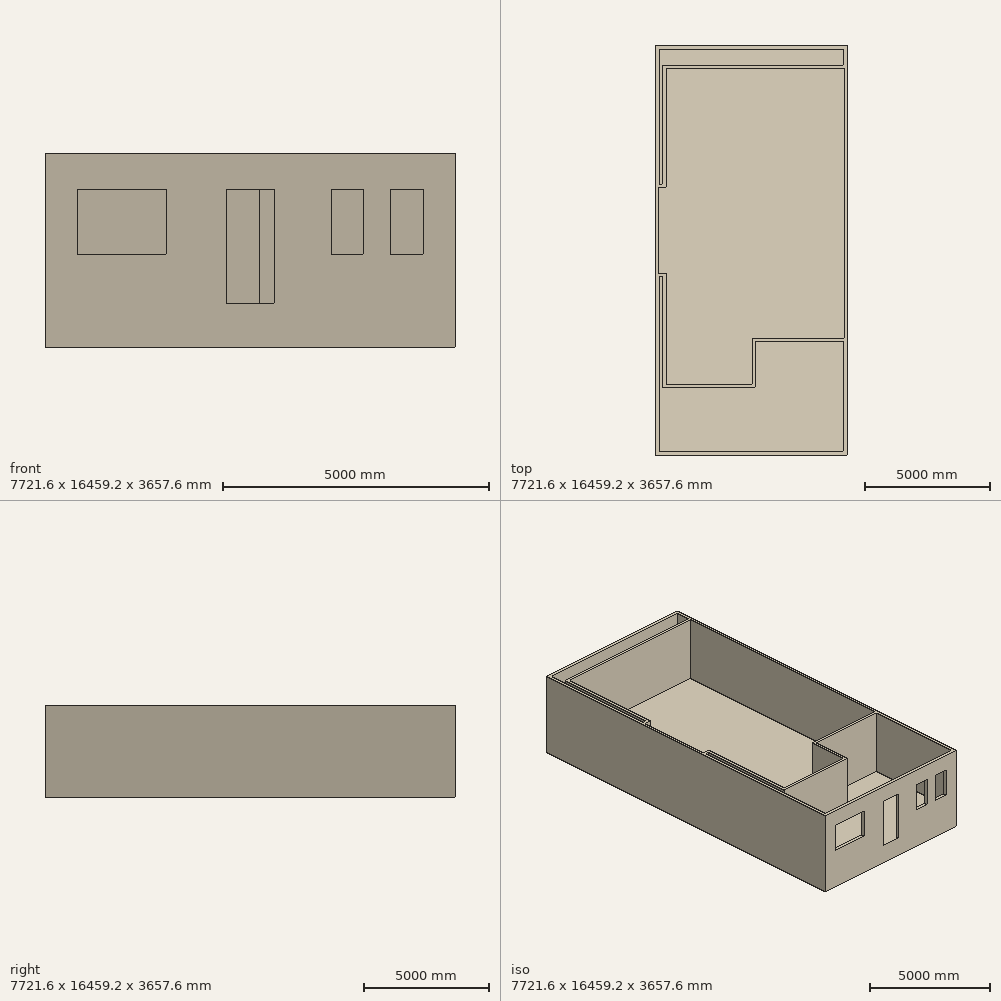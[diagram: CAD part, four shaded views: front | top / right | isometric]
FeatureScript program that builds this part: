
annotation { "Feature Type Name" : "Feature", "Feature Type Description" : "" }
export const myFeature = defineFeature(function(context is Context, id is Id, definition is map)
    precondition{}
    {
        {
            var Q0;
            Q0=qCreatedBy(makeId("Top.planeOp"),FACE);
            var sketch = newSketch(context, id + "F0", { "sketchPlane" : qUnion([Q0])});
            skLineSegment(sketch, "E0", {"start": v(3683, 0) * mm, "end": v(3683, 11099.8) * mm});
            skLineSegment(sketch, "E1", {"start": v(3683, 11099.8) * mm, "end": v(-3733.8, 11099.8) * mm});
            skLineSegment(sketch, "E2", {"start": v(-3733.8, 11099.8) * mm, "end": v(-3733.8, 6324.6) * mm});
            skLineSegment(sketch, "E3", {"start": v(-3733.8, 6324.6) * mm, "end": v(-4038.6, 6324.6) * mm});
            skLineSegment(sketch, "E4", {"start": v(-4038.6, 6324.6) * mm, "end": v(-4038.6, 2616.2) * mm});
            skLineSegment(sketch, "E5", {"start": v(-4038.6, 2616.2) * mm, "end": v(-3733.8, 2616.2) * mm});
            skLineSegment(sketch, "E6", {"start": v(-3733.8, 2616.2) * mm, "end": v(-3733.8, -1828.8) * mm});
            skLineSegment(sketch, "E7", {"start": v(0, -1828.8) * mm, "end": v(0, 0) * mm});
            skLineSegment(sketch, "E8", {"start": v(0, 0) * mm, "end": v(3683, 0) * mm});
            skPoint(sketch, "E9.orphan", {"position": v(3683, 0) * mm});
            skLineSegment(sketch, "E10", {"start": v(-3733.8, -1828.8) * mm, "end": v(0, -1828.8) * mm});
            skLineSegment(sketch, "E11.0", {"start": v(-127, -1701.8) * mm, "end": v(-127, 127) * mm});
            skLineSegment(sketch, "E11.1", {"start": v(-3606.8, -1701.8) * mm, "end": v(-127, -1701.8) * mm});
            skLineSegment(sketch, "E11.2", {"start": v(-3606.8, 2743.2) * mm, "end": v(-3606.8, -1701.8) * mm});
            skLineSegment(sketch, "E11.3", {"start": v(-3911.6, 2743.2) * mm, "end": v(-3606.8, 2743.2) * mm});
            skLineSegment(sketch, "E11.4", {"start": v(-3911.6, 6197.6) * mm, "end": v(-3911.6, 2743.2) * mm});
            skLineSegment(sketch, "E11.5", {"start": v(-127, 127) * mm, "end": v(3556, 127) * mm});
            skLineSegment(sketch, "E11.6", {"start": v(-3606.8, 6197.6) * mm, "end": v(-3911.6, 6197.6) * mm});
            skLineSegment(sketch, "E11.7", {"start": v(-3606.8, 10972.8) * mm, "end": v(-3606.8, 6197.6) * mm});
            skLineSegment(sketch, "E11.8", {"start": v(3556, 10972.8) * mm, "end": v(-3606.8, 10972.8) * mm});
            skLineSegment(sketch, "E11.9", {"start": v(3556, 127) * mm, "end": v(3556, 10972.8) * mm});
            skLineSegment(sketch, "E12.bottom", {"start": v(-3746.5, 438.15) * mm, "end": v(-3594.1, 438.15) * mm, "construction": true});
            skLineSegment(sketch, "E12.top", {"start": v(-3746.5, 1352.55) * mm, "end": v(-3594.1, 1352.55) * mm, "construction": true});
            skLineSegment(sketch, "E12.left", {"start": v(-3746.5, 438.15) * mm, "end": v(-3746.5, 1352.55) * mm, "construction": true});
            skLineSegment(sketch, "E12.right", {"start": v(-3594.1, 438.15) * mm, "end": v(-3594.1, 1352.55) * mm, "construction": true});
            skLineSegment(sketch, "E13", {"start": v(-3606.8, 2609.85) * mm, "end": v(-2933.7, 2609.85) * mm, "construction": true});
            skLineSegment(sketch, "E14", {"start": v(-2933.7, 2609.85) * mm, "end": v(-2933.7, 2743.2) * mm, "construction": true});
            skLineSegment(sketch, "E15", {"start": v(-2933.7, 2743.2) * mm, "end": v(-3606.8, 2743.2) * mm, "construction": true});
            skLineSegment(sketch, "E16.bottom", {"start": v(-2705.1, -1689.1) * mm, "end": v(-1054.1, -1689.1) * mm, "construction": true});
            skLineSegment(sketch, "E16.top", {"start": v(-2705.1, -1841.5) * mm, "end": v(-1054.1, -1841.5) * mm, "construction": true});
            skLineSegment(sketch, "E16.left", {"start": v(-2705.1, -1689.1) * mm, "end": v(-2705.1, -1841.5) * mm, "construction": true});
            skLineSegment(sketch, "E16.right", {"start": v(-1054.1, -1689.1) * mm, "end": v(-1054.1, -1841.5) * mm, "construction": true});
            skLineSegment(sketch, "E17", {"start": v(-127, 127) * mm, "end": v(-127, 2609.85) * mm, "construction": true});
            skLineSegment(sketch, "E18", {"start": v(-127, 2609.85) * mm, "end": v(-800.1, 2609.85) * mm, "construction": true});
            skLineSegment(sketch, "E19", {"start": v(-800.1, 2743.2) * mm, "end": v(-88.9, 2743.2) * mm, "construction": true});
            skLineSegment(sketch, "E20", {"start": v(-88.9, 2743.2) * mm, "end": v(660.4, 3359.05) * mm, "construction": true});
            skLineSegment(sketch, "E21", {"start": v(660.4, 3359.05) * mm, "end": v(660.4, 5268.85) * mm, "construction": true});
            skLineSegment(sketch, "E22", {"start": v(0, 127) * mm, "end": v(0, 2680.36) * mm, "construction": true});
            skLineSegment(sketch, "E23", {"start": v(76.33, 2747.5) * mm, "end": v(800.1, 1866.9) * mm, "construction": true});
            skLineSegment(sketch, "E24", {"start": v(800.1, 1866.9) * mm, "end": v(800.1, 127) * mm, "construction": true});
            skLineSegment(sketch, "E25", {"start": v(-800.1, 2743.2) * mm, "end": v(-800.1, 2609.85) * mm});
            skLineSegment(sketch, "E26", {"start": v(76.33, 2747.5) * mm, "end": v(812.8, 3352.8) * mm, "construction": true});
            skLineSegment(sketch, "E27", {"start": v(812.8, 3352.8) * mm, "end": v(3556, 3352.8) * mm, "construction": true});
            skLineSegment(sketch, "E28", {"start": v(3556, 3479.8) * mm, "end": v(787.4, 3479.8) * mm, "construction": true});
            skLineSegment(sketch, "E29", {"start": v(787.4, 3479.8) * mm, "end": v(787.4, 5181.6) * mm, "construction": true});
            skLineSegment(sketch, "E30", {"start": v(787.4, 5181.6) * mm, "end": v(3556, 5181.6) * mm, "construction": true});
            skLineSegment(sketch, "E31", {"start": v(3541.89, 5308.6) * mm, "end": v(781.97, 5308.6) * mm, "construction": true});
            skLineSegment(sketch, "E32", {"start": v(781.97, 5308.6) * mm, "end": v(0, 5845.85) * mm, "construction": true});
            skLineSegment(sketch, "E33", {"start": v(0, 8534.4) * mm, "end": v(698.5, 8534.4) * mm, "construction": true});
            skLineSegment(sketch, "E34", {"start": v(660.4, 5268.85) * mm, "end": v(-293.97, 5924.55) * mm, "construction": true});
            skLineSegment(sketch, "E35", {"start": v(-293.97, 5924.55) * mm, "end": v(-293.97, 6197.6) * mm, "construction": true});
            skLineSegment(sketch, "E36", {"start": v(-293.97, 6197.6) * mm, "end": v(-3606.8, 6197.6) * mm, "construction": true});
            skLineSegment(sketch, "E37.bottom", {"start": v(1346.2, 139.7) * mm, "end": v(2070.1, 139.7) * mm, "construction": true});
            skLineSegment(sketch, "E37.top", {"start": v(1346.2, -12.7) * mm, "end": v(2070.1, -12.7) * mm, "construction": true});
            skLineSegment(sketch, "E37.left", {"start": v(1346.2, 139.7) * mm, "end": v(1346.2, -12.7) * mm, "construction": true});
            skLineSegment(sketch, "E37.right", {"start": v(2070.1, 139.7) * mm, "end": v(2070.1, -12.7) * mm, "construction": true});
            skLineSegment(sketch, "E38.bottom", {"start": v(3543.3, 2781.3) * mm, "end": v(3695.7, 2781.3) * mm, "construction": true});
            skLineSegment(sketch, "E38.top", {"start": v(3543.3, 2051.05) * mm, "end": v(3695.7, 2051.05) * mm, "construction": true});
            skLineSegment(sketch, "E38.left", {"start": v(3543.3, 2781.3) * mm, "end": v(3543.3, 2051.05) * mm, "construction": true});
            skLineSegment(sketch, "E38.right", {"start": v(3695.7, 2781.3) * mm, "end": v(3695.7, 2051.05) * mm, "construction": true});
            skLineSegment(sketch, "E39", {"start": v(0, 2680.36) * mm, "end": v(698.5, 1830.5) * mm, "construction": true});
            skLineSegment(sketch, "E40", {"start": v(698.5, 1830.5) * mm, "end": v(698.5, 127) * mm, "construction": true});
            skLineSegment(sketch, "E41.bottom", {"start": v(3543.3, 4610.1) * mm, "end": v(3695.7, 4610.1) * mm, "construction": true});
            skLineSegment(sketch, "E41.top", {"start": v(3543.3, 4038.6) * mm, "end": v(3695.7, 4038.6) * mm, "construction": true});
            skLineSegment(sketch, "E41.left", {"start": v(3543.3, 4610.1) * mm, "end": v(3543.3, 4038.6) * mm, "construction": true});
            skLineSegment(sketch, "E41.right", {"start": v(3695.7, 4610.1) * mm, "end": v(3695.7, 4038.6) * mm, "construction": true});
            skLineSegment(sketch, "E42.bottom", {"start": v(635, 4394.2) * mm, "end": v(787.4, 4394.2) * mm, "construction": true});
            skLineSegment(sketch, "E42.top", {"start": v(635, 3632.2) * mm, "end": v(787.4, 3632.2) * mm, "construction": true});
            skLineSegment(sketch, "E42.left", {"start": v(635, 4394.2) * mm, "end": v(635, 3632.2) * mm, "construction": true});
            skLineSegment(sketch, "E42.right", {"start": v(787.4, 4394.2) * mm, "end": v(787.4, 3632.2) * mm, "construction": true});
            skLineSegment(sketch, "E43.bottom", {"start": v(-427.32, 6172.2) * mm, "end": v(-1189.32, 6172.2) * mm, "construction": true});
            skLineSegment(sketch, "E43.top", {"start": v(-427.32, 6324.6) * mm, "end": v(-1189.32, 6324.6) * mm, "construction": true});
            skLineSegment(sketch, "E43.left", {"start": v(-427.32, 6172.2) * mm, "end": v(-427.32, 6324.6) * mm, "construction": true});
            skLineSegment(sketch, "E43.right", {"start": v(-1189.32, 6172.2) * mm, "end": v(-1189.32, 6324.6) * mm, "construction": true});
            skLineSegment(sketch, "E44.bottom", {"start": v(-4064, 3619.5) * mm, "end": v(-3911.6, 3619.5) * mm, "construction": true});
            skLineSegment(sketch, "E44.top", {"start": v(-4064, 4349.75) * mm, "end": v(-3911.6, 4349.75) * mm, "construction": true});
            skLineSegment(sketch, "E44.left", {"start": v(-4064, 3619.5) * mm, "end": v(-4064, 4349.75) * mm, "construction": true});
            skLineSegment(sketch, "E44.right", {"start": v(-3911.6, 3619.5) * mm, "end": v(-3911.6, 4349.75) * mm, "construction": true});
            skLineSegment(sketch, "E45.bottom", {"start": v(3543.3, 5867.4) * mm, "end": v(3695.7, 5867.4) * mm, "construction": true});
            skLineSegment(sketch, "E45.top", {"start": v(3543.3, 7061.2) * mm, "end": v(3695.7, 7061.2) * mm, "construction": true});
            skLineSegment(sketch, "E45.left", {"start": v(3543.3, 5867.4) * mm, "end": v(3543.3, 7061.2) * mm, "construction": true});
            skLineSegment(sketch, "E45.right", {"start": v(3695.7, 5867.4) * mm, "end": v(3695.7, 7061.2) * mm, "construction": true});
            skLineSegment(sketch, "E46.bottom", {"start": v(3543.3, 9438.28) * mm, "end": v(3695.7, 9438.28) * mm, "construction": true});
            skLineSegment(sketch, "E46.top", {"start": v(3543.3, 10256.66) * mm, "end": v(3695.7, 10256.66) * mm, "construction": true});
            skLineSegment(sketch, "E46.left", {"start": v(3543.3, 9438.28) * mm, "end": v(3543.3, 10256.66) * mm, "construction": true});
            skLineSegment(sketch, "E46.right", {"start": v(3695.7, 9438.28) * mm, "end": v(3695.7, 10256.66) * mm, "construction": true});
            skLineSegment(sketch, "E47.bottom", {"start": v(2881.46, 10778.72) * mm, "end": v(1984.95, 10778.72) * mm, "construction": true});
            skLineSegment(sketch, "E47.top", {"start": v(2881.46, 10931.12) * mm, "end": v(1984.95, 10931.12) * mm, "construction": true});
            skLineSegment(sketch, "E47.left", {"start": v(2881.46, 10778.72) * mm, "end": v(2881.46, 10931.12) * mm, "construction": true});
            skLineSegment(sketch, "E47.right", {"start": v(1984.95, 10778.72) * mm, "end": v(1984.95, 10931.12) * mm, "construction": true});
            skLineSegment(sketch, "E48.bottom", {"start": v(1766.71, 10778.72) * mm, "end": v(966.52, 10778.72) * mm, "construction": true});
            skLineSegment(sketch, "E48.top", {"start": v(1766.71, 10931.12) * mm, "end": v(966.52, 10931.12) * mm, "construction": true});
            skLineSegment(sketch, "E48.left", {"start": v(1766.71, 10778.72) * mm, "end": v(1766.71, 10931.12) * mm, "construction": true});
            skLineSegment(sketch, "E48.right", {"start": v(966.52, 10778.72) * mm, "end": v(966.52, 10931.12) * mm, "construction": true});
            skLineSegment(sketch, "E49.bottom", {"start": v(-1415.88, 10778.72) * mm, "end": v(-2525.25, 10778.72) * mm, "construction": true});
            skLineSegment(sketch, "E49.top", {"start": v(-1415.88, 10931.12) * mm, "end": v(-2525.25, 10931.12) * mm, "construction": true});
            skLineSegment(sketch, "E49.left", {"start": v(-1415.88, 10778.72) * mm, "end": v(-1415.88, 10931.12) * mm, "construction": true});
            skLineSegment(sketch, "E49.right", {"start": v(-2525.25, 10778.72) * mm, "end": v(-2525.25, 10931.12) * mm, "construction": true});
            skPoint(sketch, "E50.oppositeSnap0", {"position": v(-3606.8, 8585.2) * mm});
            skLineSegment(sketch, "E50.bottom", {"start": v(-3936.87, 7828.6) * mm, "end": v(-4089.27, 7828.6) * mm, "construction": true});
            skLineSegment(sketch, "E50.top", {"start": v(-3936.87, 8585.2) * mm, "end": v(-4089.27, 8585.2) * mm, "construction": true});
            skLineSegment(sketch, "E50.left", {"start": v(-3936.87, 7828.6) * mm, "end": v(-3936.87, 8585.2) * mm, "construction": true});
            skLineSegment(sketch, "E50.right", {"start": v(-4089.27, 7828.6) * mm, "end": v(-4089.27, 8585.2) * mm, "construction": true});
            skLineSegment(sketch, "E51", {"start": v(-3606.8, 6299.2) * mm, "end": v(-293.97, 6299.2) * mm, "construction": true});
            skLineSegment(sketch, "E52", {"start": v(-293.97, 6299.2) * mm, "end": v(-293.97, 9093.2) * mm, "construction": true});
            skLineSegment(sketch, "E53", {"start": v(-293.97, 9093.2) * mm, "end": v(-805.07, 9093.2) * mm, "construction": true});
            skLineSegment(sketch, "E54", {"start": v(-805.07, 9093.2) * mm, "end": v(-805.07, 9245.6) * mm, "construction": true});
            skLineSegment(sketch, "E55", {"start": v(-805.07, 9245.6) * mm, "end": v(-293.97, 9245.6) * mm, "construction": true});
            skLineSegment(sketch, "E56", {"start": v(-293.97, 9245.6) * mm, "end": v(-293.97, 10972.8) * mm, "construction": true});
            skLineSegment(sketch, "E57", {"start": v(-107.65, 5765.72) * mm, "end": v(520.4, 5334.22) * mm, "construction": true});
            skLineSegment(sketch, "E58", {"start": v(520.4, 5334.22) * mm, "end": v(606.7, 5459.83) * mm, "construction": true});
            skLineSegment(sketch, "E59", {"start": v(606.7, 5459.83) * mm, "end": v(-21.35, 5891.33) * mm, "construction": true});
            skLineSegment(sketch, "E60", {"start": v(-21.35, 5891.33) * mm, "end": v(-107.65, 5765.72) * mm, "construction": true});
            skLineSegment(sketch, "E61", {"start": v(50.34, 2893.8) * mm, "end": v(639.02, 3377.65) * mm, "construction": true});
            skLineSegment(sketch, "E62", {"start": v(639.02, 3377.65) * mm, "end": v(735.79, 3259.91) * mm, "construction": true});
            skLineSegment(sketch, "E63", {"start": v(735.79, 3259.91) * mm, "end": v(147.1, 2776.07) * mm, "construction": true});
            skLineSegment(sketch, "E64", {"start": v(147.1, 2776.07) * mm, "end": v(50.34, 2893.8) * mm, "construction": true});
            skLineSegment(sketch, "E65", {"start": v(800.1, 8534.4) * mm, "end": v(800.1, 7010.4) * mm, "construction": true});
            skLineSegment(sketch, "E66", {"start": v(800.1, 7010.4) * mm, "end": v(0, 5845.85) * mm, "construction": true});
            skLineSegment(sketch, "E67", {"start": v(0, 6025.27) * mm, "end": v(698.5, 7041.94) * mm, "construction": true});
            skLineSegment(sketch, "E68", {"start": v(698.5, 7041.94) * mm, "end": v(698.5, 8534.4) * mm, "construction": true});
            skLineSegment(sketch, "E69.bottom", {"start": v(-4064, 4527.55) * mm, "end": v(-3911.6, 4527.55) * mm, "construction": true});
            skLineSegment(sketch, "E69.top", {"start": v(-4064, 5257.8) * mm, "end": v(-3911.6, 5257.8) * mm, "construction": true});
            skLineSegment(sketch, "E69.left", {"start": v(-4064, 4527.55) * mm, "end": v(-4064, 5257.8) * mm, "construction": true});
            skLineSegment(sketch, "E69.right", {"start": v(-3911.6, 4527.55) * mm, "end": v(-3911.6, 5257.8) * mm, "construction": true});
            skLineSegment(sketch, "E70.trimOffspring", {"start": v(800.1, 8534.4) * mm, "end": v(3556, 8534.4) * mm, "construction": true});
            skLineSegment(sketch, "E71", {"start": v(0, 8686.8) * mm, "end": v(3556, 8686.8) * mm, "construction": true});
            skLineSegment(sketch, "E72.trimOffspring", {"start": v(0, 6025.27) * mm, "end": v(0, 8534.4) * mm, "construction": true});
            skLineSegment(sketch, "E73.trimOffspring", {"start": v(0, 8686.8) * mm, "end": v(0, 10972.8) * mm, "construction": true});
            skSolve(sketch);
        }
        {
            var Q0;
            Q0=qSketchRegion(id+"F0",true);
            extrude(context, id + "F1", {"entities" : qUnion([Q0]), "depth" : 3657.6 * mm});
        }
        {
            var Q0;
            Q0=qCreatedBy(makeId("Top.planeOp"),FACE);
            var sketch = newSketch(context, id + "F2", { "sketchPlane" : qUnion([Q0])});
            skLineSegment(sketch, "E74.bottom", {"start": v(3683, -4572) * mm, "end": v(-4038.6, -4572) * mm});
            skLineSegment(sketch, "E74.top", {"start": v(3683, 11887.2) * mm, "end": v(-4038.6, 11887.2) * mm});
            skLineSegment(sketch, "E74.left", {"start": v(3683, -4572) * mm, "end": v(3683, 0) * mm});
            skLineSegment(sketch, "E74.right", {"start": v(-4038.6, -4572) * mm, "end": v(-4038.6, 2616.2) * mm});
            skLineSegment(sketch, "E75.0", {"start": v(3530.6, 11734.8) * mm, "end": v(-3886.2, 11734.8) * mm});
            skLineSegment(sketch, "E75.1", {"start": v(-3886.2, -4419.6) * mm, "end": v(-3886.2, 2616.2) * mm});
            skLineSegment(sketch, "E75.2", {"start": v(3530.6, -4419.6) * mm, "end": v(-3886.2, -4419.6) * mm});
            skLineSegment(sketch, "E75.3", {"start": v(3530.6, -4419.6) * mm, "end": v(3530.6, 0) * mm});
            skLineSegment(sketch, "E76", {"start": v(3530.6, 0) * mm, "end": v(3683, 0) * mm});
            skLineSegment(sketch, "E77", {"start": v(-4038.6, 2616.2) * mm, "end": v(-3886.2, 2616.2) * mm});
            skLineSegment(sketch, "E78", {"start": v(-4038.6, 6324.6) * mm, "end": v(-3886.2, 6324.6) * mm});
            skLineSegment(sketch, "E79.trimOffspring", {"start": v(-3886.2, 6324.6) * mm, "end": v(-3886.2, 11734.8) * mm});
            skLineSegment(sketch, "E80.trimOffspring", {"start": v(-4038.6, 6324.6) * mm, "end": v(-4038.6, 11887.2) * mm});
            skLineSegment(sketch, "E81", {"start": v(3683, 11887.2) * mm, "end": v(3683, 11099.8) * mm});
            skLineSegment(sketch, "E82", {"start": v(3683, 11099.8) * mm, "end": v(3530.6, 11099.8) * mm});
            skLineSegment(sketch, "E83", {"start": v(3530.6, 11099.8) * mm, "end": v(3530.6, 11734.8) * mm});
            skSolve(sketch);
        }
        {
            var Q0;
            Q0=qSketchRegion(id+"F2",true);
            extrude(context, id + "F3", {"entities" : qUnion([Q0]), "operationType" : NewBodyOperationType.ADD, "depth" : 762 * mm});
        }
        {
            var Q0;
            Q0=makeQuery(id+"F3.opExtrude","CAP_FACE",FACE,{"disambiguationData":[OSD([sQuery(id+"F2.wireOp",EDGE,"E74.bottom"),sQuery(id+"F2.wireOp",EDGE,"E74.left"),sQuery(id+"F2.wireOp",EDGE,"E74.right"),sQuery(id+"F2.wireOp",EDGE,"E75.1"),sQuery(id+"F2.wireOp",EDGE,"E75.2"),sQuery(id+"F2.wireOp",EDGE,"E75.3"),sQuery(id+"F2.wireOp",EDGE,"E76"),sQuery(id+"F2.wireOp",EDGE,"E77")])],"isStart":false});
            var sketch = newSketch(context, id + "F4", { "sketchPlane" : qUnion([Q0])});
            skLineSegment(sketch, "E84.0", {"start": v(3683, -4572) * mm, "end": v(3683, 0) * mm});
            skLineSegment(sketch, "E85.0", {"start": v(3683, -4572) * mm, "end": v(-4038.6, -4572) * mm});
            skLineSegment(sketch, "E86.1", {"start": v(-4038.6, -4572) * mm, "end": v(-4038.6, 2616.2) * mm});
            skLineSegment(sketch, "E87.2", {"start": v(-4038.6, 6324.6) * mm, "end": v(-4038.6, 2616.2) * mm});
            skLineSegment(sketch, "E88.3", {"start": v(-4038.6, 6324.6) * mm, "end": v(-4038.6, 11887.2) * mm});
            skLineSegment(sketch, "E89.4", {"start": v(3683, 11887.2) * mm, "end": v(-4038.6, 11887.2) * mm});
            skLineSegment(sketch, "E89.5", {"start": v(3683, 0) * mm, "end": v(3683, 11099.8) * mm});
            skLineSegment(sketch, "E90.0", {"start": v(3683, 11887.2) * mm, "end": v(3683, 11099.8) * mm});
            skSolve(sketch);
        }
        {
            var Q0;
            Q0=qSketchRegion(id+"F4",true);
            extrude(context, id + "F5", {"entities" : qUnion([Q0]), "operationType" : NewBodyOperationType.ADD, "depth" : 76.2 * mm});
        }
        {
            var Q0;
            {var subQ0=sQuery(id+"F4.wireOp",EDGE,"E84.0");var subQ1=sQuery(id+"F4.wireOp",EDGE,"E85.0");var subQ2=sQuery(id+"F4.wireOp",EDGE,"E86.1");var subQ3=sQuery(id+"F4.wireOp",EDGE,"E87.2");var subQ4=sQuery(id+"F4.wireOp",EDGE,"E88.3");var subQ5=sQuery(id+"F4.wireOp",EDGE,"E89.5");var subQ6=sQuery(id+"F4.wireOp",EDGE,"E90.0");Q0=makeQuery(id+"F5.boolean.opBoolean","SPLIT",FACE,{"disambiguationData":[TD([makeQuery(id+"F1.opExtrude","SWEPT_FACE",FACE,{"disambiguationData":[OSD([sQuery(id+"F0.wireOp",EDGE,"E5")])]})])],"derivedFrom":makeQuery(id+"F5.opExtrude","CAP_FACE",FACE,{"disambiguationData":[OSD([subQ0,subQ1,subQ2,subQ3,subQ4,sQuery(id+"F4.wireOp",EDGE,"E89.4"),subQ5,subQ6])],"isStart":false})});}
            var sketch = newSketch(context, id + "F6", { "sketchPlane" : qUnion([Q0])});
            skLineSegment(sketch, "E91.0", {"start": v(3683, -4572) * mm, "end": v(-4038.6, -4572) * mm});
            skLineSegment(sketch, "E91.1", {"start": v(3683, 11887.2) * mm, "end": v(-4038.6, 11887.2) * mm});
            skLineSegment(sketch, "E91.2", {"start": v(3683, -4572) * mm, "end": v(3683, 0) * mm});
            skLineSegment(sketch, "E91.3", {"start": v(-4038.6, -4572) * mm, "end": v(-4038.6, 2616.2) * mm});
            skLineSegment(sketch, "E91.4", {"start": v(3530.6, 11734.8) * mm, "end": v(-3886.2, 11734.8) * mm});
            skLineSegment(sketch, "E91.5", {"start": v(-3886.2, -4419.6) * mm, "end": v(-3886.2, 2616.2) * mm});
            skLineSegment(sketch, "E91.6", {"start": v(3530.6, -4419.6) * mm, "end": v(-3886.2, -4419.6) * mm});
            skLineSegment(sketch, "E91.7", {"start": v(3530.6, -4419.6) * mm, "end": v(3530.6, 0) * mm});
            skLineSegment(sketch, "E91.8", {"start": v(3530.6, 0) * mm, "end": v(3683, 0) * mm});
            skLineSegment(sketch, "E91.9", {"start": v(-4038.6, 2616.2) * mm, "end": v(-3886.2, 2616.2) * mm});
            skLineSegment(sketch, "E91.10", {"start": v(-4038.6, 6324.6) * mm, "end": v(-3886.2, 6324.6) * mm});
            skLineSegment(sketch, "E91.11", {"start": v(-3886.2, 6324.6) * mm, "end": v(-3886.2, 11734.8) * mm});
            skLineSegment(sketch, "E91.12", {"start": v(-4038.6, 6324.6) * mm, "end": v(-4038.6, 11887.2) * mm});
            skLineSegment(sketch, "E91.13", {"start": v(3683, 11887.2) * mm, "end": v(3683, 11099.8) * mm});
            skLineSegment(sketch, "E91.14", {"start": v(3683, 11099.8) * mm, "end": v(3530.6, 11099.8) * mm});
            skLineSegment(sketch, "E91.15", {"start": v(3530.6, 11099.8) * mm, "end": v(3530.6, 11734.8) * mm});
            skSolve(sketch);
        }
        {
            var Q0;
            Q0=qSketchRegion(id+"F2",true);
            var Q1;
            Q1=makeQuery(id+"F1.opExtrude","CAP_FACE",FACE,{"disambiguationData":[OSD([sQuery(id+"F0.wireOp",EDGE,"E0"),sQuery(id+"F0.wireOp",EDGE,"E1"),sQuery(id+"F0.wireOp",EDGE,"E2"),sQuery(id+"F0.wireOp",EDGE,"E3"),sQuery(id+"F0.wireOp",EDGE,"E4"),sQuery(id+"F0.wireOp",EDGE,"E5"),sQuery(id+"F0.wireOp",EDGE,"E6"),sQuery(id+"F0.wireOp",EDGE,"E7"),sQuery(id+"F0.wireOp",EDGE,"E8"),sQuery(id+"F0.wireOp",EDGE,"E10"),sQuery(id+"F0.wireOp",EDGE,"E11.0"),sQuery(id+"F0.wireOp",EDGE,"E11.1"),sQuery(id+"F0.wireOp",EDGE,"E11.2"),sQuery(id+"F0.wireOp",EDGE,"E11.3"),sQuery(id+"F0.wireOp",EDGE,"E11.4"),sQuery(id+"F0.wireOp",EDGE,"E11.5"),sQuery(id+"F0.wireOp",EDGE,"E11.6"),sQuery(id+"F0.wireOp",EDGE,"E11.7"),sQuery(id+"F0.wireOp",EDGE,"E11.8"),sQuery(id+"F0.wireOp",EDGE,"E11.9")])],"isStart":false});
            extrude(context, id + "F7", {"entities" : qUnion([Q0]), "operationType" : NewBodyOperationType.ADD, "endBound" : BoundingType.UP_TO_SURFACE, "endBoundEntityFace" : qUnion([Q1]), "depth" : 25.4 * mm});
        }
        {
            var Q0;
            {var subQ0=sQuery(id+"F2.wireOp",EDGE,"E74.bottom");Q0=makeQuery(id+"F7.boolean.opBoolean","MERGE",FACE,{"derivedFrom":[makeQuery(id+"F5.boolean.opBoolean","MERGE",FACE,{"derivedFrom":[makeQuery(id+"F3.opExtrude","SWEPT_FACE",FACE,{"disambiguationData":[OSD([subQ0])]}),makeQuery(id+"F5.opExtrude","SWEPT_FACE",FACE,{"disambiguationData":[OSD([sQuery(id+"F4.wireOp",EDGE,"E85.0")])]})]}),makeQuery(id+"F7.opExtrude","SWEPT_FACE",FACE,{"disambiguationData":[OSD([subQ0])]})]});}
            var sketch = newSketch(context, id + "F8", { "sketchPlane" : qUnion([Q0])});
            skLineSegment(sketch, "E92.bottom", {"start": v(-3429, 2971.8) * mm, "end": v(-1752.6, 2971.8) * mm});
            skLineSegment(sketch, "E92.top", {"start": v(-3429, 1752.6) * mm, "end": v(-1752.6, 1752.6) * mm});
            skLineSegment(sketch, "E92.left", {"start": v(-3429, 2971.8) * mm, "end": v(-3429, 1752.6) * mm});
            skLineSegment(sketch, "E92.right", {"start": v(-1752.6, 2971.8) * mm, "end": v(-1752.6, 1752.6) * mm});
            skLineSegment(sketch, "E93.bottom", {"start": v(-635, 838.2) * mm, "end": v(279.4, 838.2) * mm});
            skLineSegment(sketch, "E93.top", {"start": v(-635, 2971.8) * mm, "end": v(279.4, 2971.8) * mm});
            skLineSegment(sketch, "E93.left", {"start": v(-635, 838.2) * mm, "end": v(-635, 2971.8) * mm});
            skLineSegment(sketch, "E93.right", {"start": v(279.4, 838.2) * mm, "end": v(279.4, 2971.8) * mm});
            skLineSegment(sketch, "E94.bottom", {"start": v(2463.8, 2971.8) * mm, "end": v(3073.4, 2971.8) * mm});
            skLineSegment(sketch, "E94.top", {"start": v(2463.8, 1752.6) * mm, "end": v(3073.4, 1752.6) * mm});
            skLineSegment(sketch, "E94.left", {"start": v(2463.8, 2971.8) * mm, "end": v(2463.8, 1752.6) * mm});
            skLineSegment(sketch, "E94.right", {"start": v(3073.4, 2971.8) * mm, "end": v(3073.4, 1752.6) * mm});
            skLineSegment(sketch, "E95.bottom", {"start": v(1346.2, 1752.6) * mm, "end": v(1955.8, 1752.6) * mm});
            skLineSegment(sketch, "E95.top", {"start": v(1346.2, 2971.8) * mm, "end": v(1955.8, 2971.8) * mm});
            skLineSegment(sketch, "E95.left", {"start": v(1346.2, 1752.6) * mm, "end": v(1346.2, 2971.8) * mm});
            skLineSegment(sketch, "E95.right", {"start": v(1955.8, 1752.6) * mm, "end": v(1955.8, 2971.8) * mm});
            skSolve(sketch);
        }
        {
            var Q0;
            Q0=qSketchRegion(id+"F8",true);
            extrude(context, id + "F9", {"entities" : qUnion([Q0]), "operationType" : NewBodyOperationType.REMOVE, "endBound" : BoundingType.UP_TO_NEXT, "oppositeDirection" : true, "depth" : 25.4 * mm});
        }
    });
